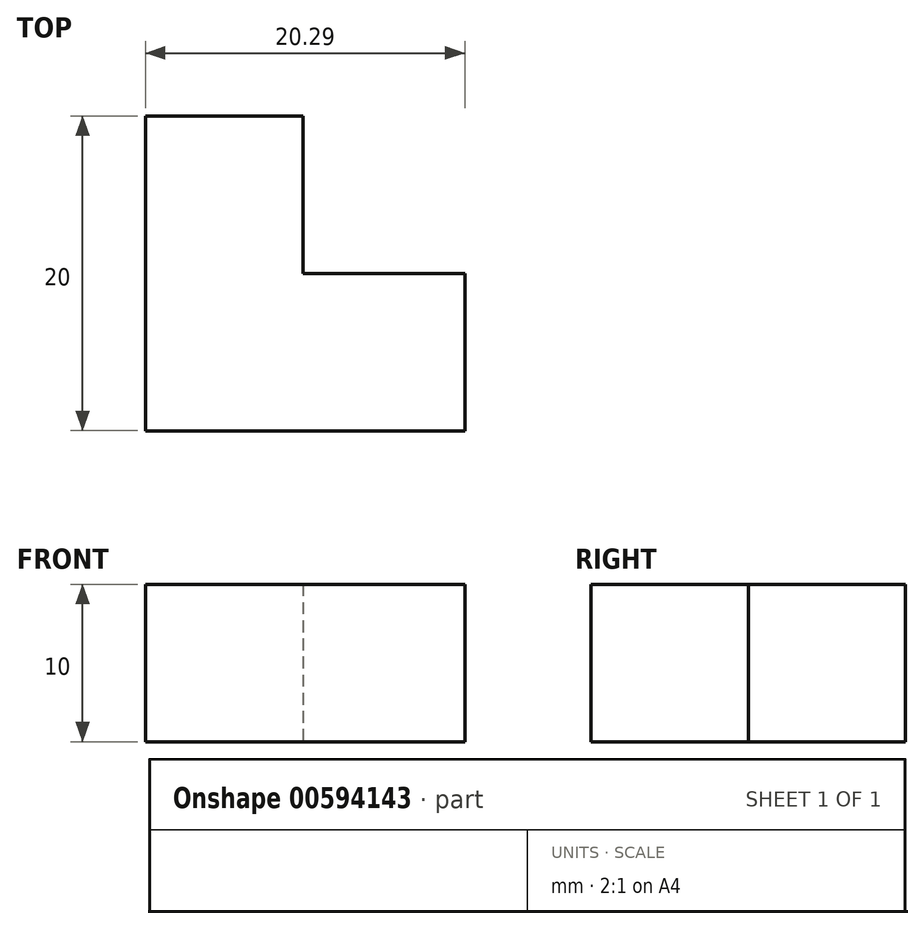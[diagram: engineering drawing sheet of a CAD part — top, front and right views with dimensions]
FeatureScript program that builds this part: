
annotation { "Feature Type Name" : "Feature", "Feature Type Description" : "" }
export const myFeature = defineFeature(function(context is Context, id is Id, definition is map)
    precondition{}
    {
        {
            var Q0;
            Q0=qCreatedBy(makeId("Top.planeOp"),FACE);
            var sketch = newSketch(context, id + "F0", { "sketchPlane" : qUnion([Q0])});
            skLineSegment(sketch, "E0", {"start": v(-32.98, 18.23) * mm, "end": v(-32.98, 38.23) * mm});
            skLineSegment(sketch, "E1", {"start": v(-32.98, 38.23) * mm, "end": v(-22.98, 38.23) * mm});
            skLineSegment(sketch, "E2", {"start": v(-22.98, 38.23) * mm, "end": v(-22.98, 28.23) * mm});
            skLineSegment(sketch, "E3", {"start": v(-22.98, 28.23) * mm, "end": v(-12.7, 28.23) * mm});
            skLineSegment(sketch, "E4", {"start": v(-12.7, 28.23) * mm, "end": v(-12.7, 18.23) * mm});
            skLineSegment(sketch, "E5", {"start": v(-12.7, 18.23) * mm, "end": v(-32.98, 18.23) * mm});
            skSolve(sketch);
        }
        {
            var Q0;
            Q0 = qSketchRegion(id + "F0", true);
            extrude(context, id + "F1", {"entities" : qUnion([Q0]), "depth" : 10 * mm, "offsetDistance" : 25 * mm});
        }
        {
            var Q0;
            Q0=makeQuery(id+"F0.imprint","IMPRINT",FACE,{"disambiguationData":[TD([[makeQuery(id+"F0.imprint","IMPRINT",EDGE,{"derivedFrom":sQuery(id+"F0.wireOp",EDGE,"E0")}),-1.0]])]});
            var Q1;
            Q1=makeQuery(id+"F0.imprint","IMPRINT",FACE,{"disambiguationData":[TD([[makeQuery(id+"F0.imprint","IMPRINT",EDGE,{"derivedFrom":sQuery(id+"F0.wireOp",EDGE,"E0")}),-1.0]])]});
            extrude(context, id + "F2", {"entities" : qUnion([Q0, Q1]), "depth" : 10 * mm, "offsetDistance" : 25 * mm});
        }
    });
